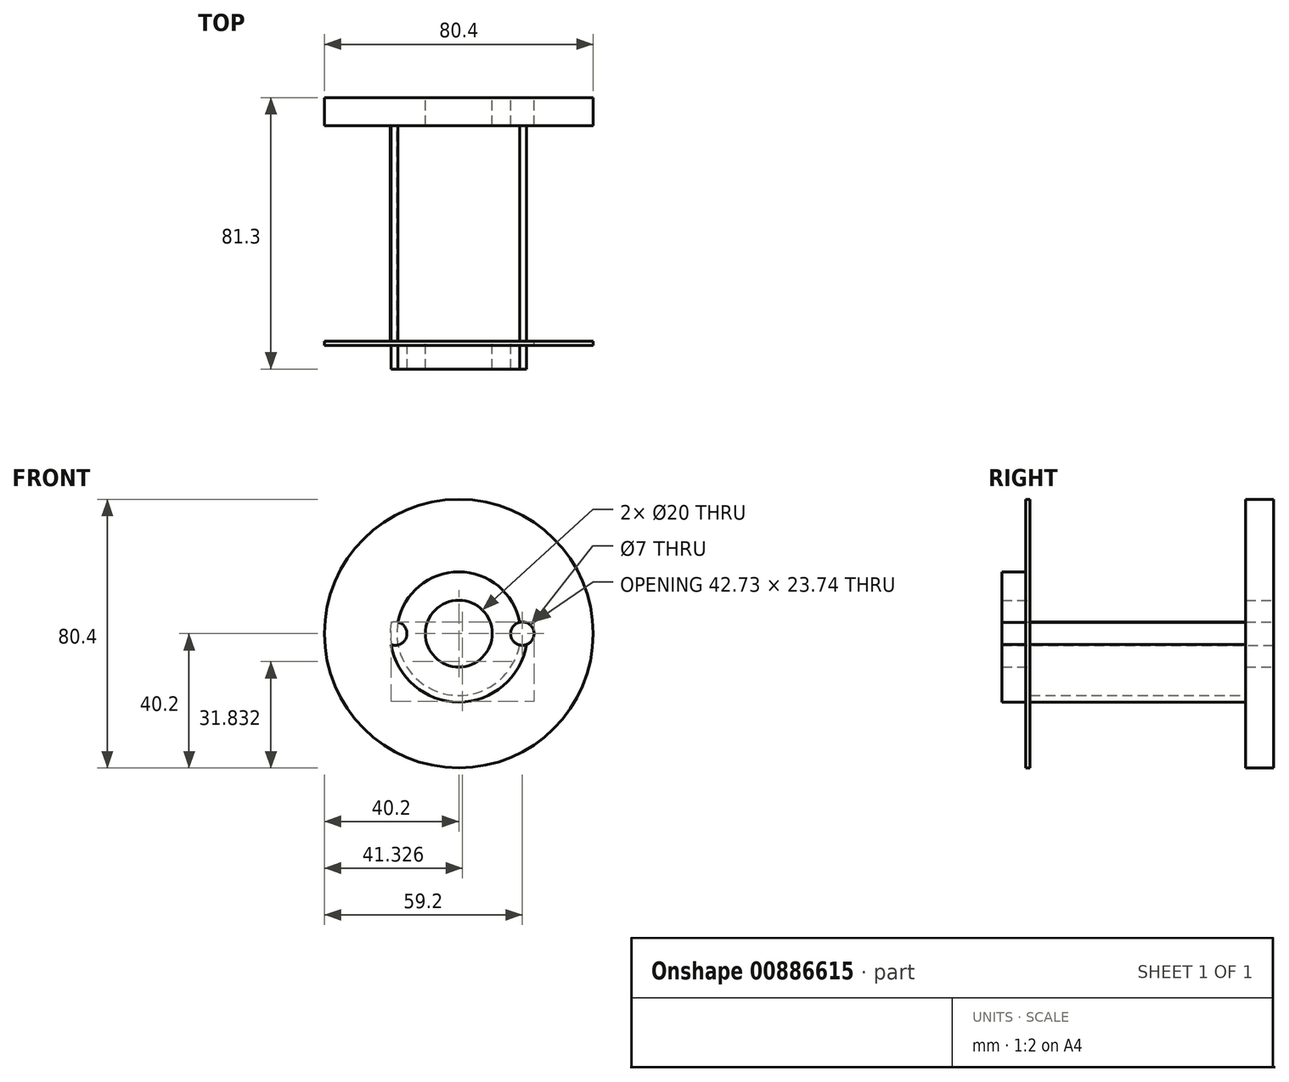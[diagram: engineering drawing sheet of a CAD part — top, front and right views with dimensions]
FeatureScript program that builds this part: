
annotation { "Feature Type Name" : "Feature", "Feature Type Description" : "" }
export const myFeature = defineFeature(function(context is Context, id is Id, definition is map)
    precondition{}
    {
        {
            var Q0;
            Q0=qCreatedBy(makeId("Front.planeOp"),FACE);
            var sketch = newSketch(context, id + "F0", { "sketchPlane" : qUnion([Q0])});
            skCircle(sketch, "E0", {"center": v(0, 0) * mm, "radius": 40.2 * mm});
            skCircle(sketch, "E1", {"center": v(0, 0) * mm, "radius": 10 * mm});
            skCircle(sketch, "E2", {"center": v(-19, 0) * mm, "radius": 3.5 * mm});
            skCircle(sketch, "E3.MirrorC", {"center": v(19, 0) * mm, "radius": 3.5 * mm});
            skCircle(sketch, "E4", {"center": v(0, 0) * mm, "radius": 20.5 * mm});
            skCircle(sketch, "E5.0", {"center": v(0, 0) * mm, "radius": 18.5 * mm});
            skSolve(sketch);
        }
        {
            var Q0;
            Q0=makeQuery(id+"F0.imprint","IMPRINT",FACE,{"disambiguationData":[TD([[makeQuery(id+"F0.imprint","IMPRINT",EDGE,{"derivedFrom":sQuery(id+"F0.wireOp",EDGE,"E1")}),-1.0]])]});
            var Q1;
            {var subQ0=sQuery(id+"F0.wireOp",EDGE,"E4");var subQ1=sQuery(id+"F0.wireOp",EDGE,"E3.MirrorC");var subQ2=makeQuery(id+"F0.imprint","INTERSECT",VERTEX,{"disambiguationData":[OD(0.0)],"derivedFrom":[subQ1,subQ0]});Q1=makeQuery(id+"F0.imprint","IMPRINT",FACE,{"disambiguationData":[TD([[makeQuery(id+"F0.imprint","IMPRINT",EDGE,{"disambiguationData":[TD([[subQ2,1.0]])],"derivedFrom":subQ1}),-1.0]])]});}
            var Q2;
            {var subQ0=sQuery(id+"F0.wireOp",EDGE,"E4");var subQ1=sQuery(id+"F0.wireOp",EDGE,"E3.MirrorC");var subQ2=makeQuery(id+"F0.imprint","INTERSECT",VERTEX,{"disambiguationData":[OD(0.0)],"derivedFrom":[subQ1,subQ0]});Q2=makeQuery(id+"F0.imprint","IMPRINT",FACE,{"disambiguationData":[TD([[makeQuery(id+"F0.imprint","IMPRINT",EDGE,{"disambiguationData":[TD([[subQ2,-1.0]])],"derivedFrom":subQ1}),-1.0]])]});}
            var Q3;
            Q3=makeQuery(id+"F0.imprint","IMPRINT",FACE,{"disambiguationData":[TD([[makeQuery(id+"F0.imprint","IMPRINT",EDGE,{"derivedFrom":sQuery(id+"F0.wireOp",EDGE,"E0")}),1.0]])]});
            var Q4;
            {var subQ0=sQuery(id+"F0.wireOp",EDGE,"E4");var subQ1=sQuery(id+"F0.wireOp",EDGE,"E2");var subQ2=makeQuery(id+"F0.imprint","INTERSECT",VERTEX,{"disambiguationData":[OD(0.0)],"derivedFrom":[subQ1,subQ0]});Q4=makeQuery(id+"F0.imprint","IMPRINT",FACE,{"disambiguationData":[TD([[makeQuery(id+"F0.imprint","IMPRINT",EDGE,{"disambiguationData":[TD([[subQ2,-1.0]])],"derivedFrom":subQ1}),1.0]])]});}
            var Q5;
            {var subQ0=sQuery(id+"F0.wireOp",EDGE,"E4");var subQ1=sQuery(id+"F0.wireOp",EDGE,"E2");var subQ2=makeQuery(id+"F0.imprint","INTERSECT",VERTEX,{"disambiguationData":[OD(0.0)],"derivedFrom":[subQ1,subQ0]});Q5=makeQuery(id+"F0.imprint","IMPRINT",FACE,{"disambiguationData":[TD([[makeQuery(id+"F0.imprint","IMPRINT",EDGE,{"disambiguationData":[TD([[subQ2,1.0]])],"derivedFrom":subQ1}),-1.0]])]});}
            var Q6;
            {var subQ0=sQuery(id+"F0.wireOp",EDGE,"E4");var subQ1=sQuery(id+"F0.wireOp",EDGE,"E2");var subQ2=makeQuery(id+"F0.imprint","INTERSECT",VERTEX,{"disambiguationData":[OD(0.0)],"derivedFrom":[subQ1,subQ0]});Q6=makeQuery(id+"F0.imprint","IMPRINT",FACE,{"disambiguationData":[TD([[makeQuery(id+"F0.imprint","IMPRINT",EDGE,{"disambiguationData":[TD([[subQ2,1.0]])],"derivedFrom":subQ1}),1.0]])]});}
            var Q7;
            {var subQ0=sQuery(id+"F0.wireOp",EDGE,"E5.0");var subQ1=sQuery(id+"F0.wireOp",EDGE,"E2");var subQ2=makeQuery(id+"F0.imprint","INTERSECT",VERTEX,{"disambiguationData":[OD(0.0)],"derivedFrom":[subQ1,subQ0]});Q7=makeQuery(id+"F0.imprint","IMPRINT",FACE,{"disambiguationData":[TD([[makeQuery(id+"F0.imprint","IMPRINT",EDGE,{"disambiguationData":[TD([[subQ2,1.0]])],"derivedFrom":subQ1}),1.0]])]});}
            var Q8;
            {var subQ0=sQuery(id+"F0.wireOp",EDGE,"E4");var subQ1=sQuery(id+"F0.wireOp",EDGE,"E2");var subQ2=makeQuery(id+"F0.imprint","INTERSECT",VERTEX,{"disambiguationData":[OD(1.0)],"derivedFrom":[subQ1,subQ0]});Q8=makeQuery(id+"F0.imprint","IMPRINT",FACE,{"disambiguationData":[TD([[makeQuery(id+"F0.imprint","IMPRINT",EDGE,{"disambiguationData":[TD([[subQ2,-1.0]])],"derivedFrom":subQ1}),-1.0]])]});}
            var Q9;
            {var subQ0=sQuery(id+"F0.wireOp",EDGE,"E5.0");var subQ1=sQuery(id+"F0.wireOp",EDGE,"E3.MirrorC");var subQ2=makeQuery(id+"F0.imprint","INTERSECT",VERTEX,{"disambiguationData":[OD(0.0)],"derivedFrom":[subQ1,subQ0]});Q9=makeQuery(id+"F0.imprint","IMPRINT",FACE,{"disambiguationData":[TD([[makeQuery(id+"F0.imprint","IMPRINT",EDGE,{"disambiguationData":[TD([[subQ2,1.0]])],"derivedFrom":subQ1}),-1.0]])]});}
            extrude(context, id + "F1", {"entities" : qUnion([Q0, Q1, Q2, Q3, Q4, Q5, Q6, Q7, Q8, Q9]), "endBound" : BoundingType.SYMMETRIC, "depth" : 81.3 * mm, "offsetDistance" : 25 * mm});
        }
        {
            var Q0;
            {var subQ0=sQuery(id+"F0.wireOp",EDGE,"E4");var subQ1=sQuery(id+"F0.wireOp",EDGE,"E3.MirrorC");var subQ2=makeQuery(id+"F0.imprint","INTERSECT",VERTEX,{"disambiguationData":[OD(0.0)],"derivedFrom":[subQ1,subQ0]});Q0=makeQuery(id+"F0.imprint","IMPRINT",FACE,{"disambiguationData":[TD([[makeQuery(id+"F0.imprint","IMPRINT",EDGE,{"disambiguationData":[TD([[subQ2,1.0]])],"derivedFrom":subQ1}),-1.0]])]});}
            var Q1;
            {var subQ0=sQuery(id+"F0.wireOp",EDGE,"E4");var subQ1=sQuery(id+"F0.wireOp",EDGE,"E3.MirrorC");var subQ2=makeQuery(id+"F0.imprint","INTERSECT",VERTEX,{"disambiguationData":[OD(0.0)],"derivedFrom":[subQ1,subQ0]});Q1=makeQuery(id+"F0.imprint","IMPRINT",FACE,{"disambiguationData":[TD([[makeQuery(id+"F0.imprint","IMPRINT",EDGE,{"disambiguationData":[TD([[subQ2,-1.0]])],"derivedFrom":subQ1}),-1.0]])]});}
            var Q2;
            {var subQ0=sQuery(id+"F0.wireOp",EDGE,"E4");var subQ1=sQuery(id+"F0.wireOp",EDGE,"E2");var subQ2=makeQuery(id+"F0.imprint","INTERSECT",VERTEX,{"disambiguationData":[OD(0.0)],"derivedFrom":[subQ1,subQ0]});Q2=makeQuery(id+"F0.imprint","IMPRINT",FACE,{"disambiguationData":[TD([[makeQuery(id+"F0.imprint","IMPRINT",EDGE,{"disambiguationData":[TD([[subQ2,-1.0]])],"derivedFrom":subQ1}),1.0]])]});}
            var Q3;
            {var subQ0=sQuery(id+"F0.wireOp",EDGE,"E4");var subQ1=sQuery(id+"F0.wireOp",EDGE,"E2");var subQ2=makeQuery(id+"F0.imprint","INTERSECT",VERTEX,{"disambiguationData":[OD(0.0)],"derivedFrom":[subQ1,subQ0]});Q3=makeQuery(id+"F0.imprint","IMPRINT",FACE,{"disambiguationData":[TD([[makeQuery(id+"F0.imprint","IMPRINT",EDGE,{"disambiguationData":[TD([[subQ2,1.0]])],"derivedFrom":subQ1}),1.0]])]});}
            var Q4;
            {var subQ0=sQuery(id+"F0.wireOp",EDGE,"E5.0");var subQ1=sQuery(id+"F0.wireOp",EDGE,"E2");var subQ2=makeQuery(id+"F0.imprint","INTERSECT",VERTEX,{"disambiguationData":[OD(0.0)],"derivedFrom":[subQ1,subQ0]});Q4=makeQuery(id+"F0.imprint","IMPRINT",FACE,{"disambiguationData":[TD([[makeQuery(id+"F0.imprint","IMPRINT",EDGE,{"disambiguationData":[TD([[subQ2,1.0]])],"derivedFrom":subQ1}),1.0]])]});}
            var Q5;
            {var subQ0=sQuery(id+"F0.wireOp",EDGE,"E5.0");var subQ1=sQuery(id+"F0.wireOp",EDGE,"E3.MirrorC");var subQ2=makeQuery(id+"F0.imprint","INTERSECT",VERTEX,{"disambiguationData":[OD(0.0)],"derivedFrom":[subQ1,subQ0]});Q5=makeQuery(id+"F0.imprint","IMPRINT",FACE,{"disambiguationData":[TD([[makeQuery(id+"F0.imprint","IMPRINT",EDGE,{"disambiguationData":[TD([[subQ2,1.0]])],"derivedFrom":subQ1}),-1.0]])]});}
            var Q6;
            Q6=sQuery(id+"F0.wireOp",EDGE,"E2");
            var Q7;
            Q7=sQuery(id+"F0.wireOp",EDGE,"E3.MirrorC");
            var Q8;
            Q8=makeQuery(id+"F1.opExtrude","CAP_FACE",FACE,{"disambiguationData":[OSD([sQuery(id+"F0.wireOp",EDGE,"E0"),sQuery(id+"F0.wireOp",EDGE,"E1")])],"isStart":false});
            extrude(context, id + "F2", {"entities" : qUnion([Q0, Q1, Q2, Q3, Q4, Q5]), "operationType" : NewBodyOperationType.REMOVE, "surfaceEntities" : qUnion([Q6, Q7]), "endBound" : BoundingType.UP_TO_SURFACE, "depth" : 7.2 * mm, "endBoundEntityFace" : qUnion([Q8]), "offsetDistance" : 25 * mm, "hasSecondDirection" : true, "secondDirectionOppositeDirection" : false, "secondDirectionDepth" : ((81.5 / 2) - 7.2) * mm});
        }
        {
            var Q0;
            Q0=makeQuery(id+"F0.imprint","IMPRINT",FACE,{"disambiguationData":[TD([[makeQuery(id+"F0.imprint","IMPRINT",EDGE,{"derivedFrom":sQuery(id+"F0.wireOp",EDGE,"E0")}),1.0]])]});
            var Q1;
            {var subQ0=sQuery(id+"F0.wireOp",EDGE,"E4");var subQ1=sQuery(id+"F0.wireOp",EDGE,"E2");var subQ2=makeQuery(id+"F0.imprint","INTERSECT",VERTEX,{"disambiguationData":[OD(0.0)],"derivedFrom":[subQ1,subQ0]});Q1=makeQuery(id+"F0.imprint","IMPRINT",FACE,{"disambiguationData":[TD([[makeQuery(id+"F0.imprint","IMPRINT",EDGE,{"disambiguationData":[TD([[subQ2,-1.0]])],"derivedFrom":subQ1}),1.0]])]});}
            var Q2;
            {var subQ0=sQuery(id+"F0.wireOp",EDGE,"E4");var subQ1=sQuery(id+"F0.wireOp",EDGE,"E3.MirrorC");var subQ2=makeQuery(id+"F0.imprint","INTERSECT",VERTEX,{"disambiguationData":[OD(0.0)],"derivedFrom":[subQ1,subQ0]});Q2=makeQuery(id+"F0.imprint","IMPRINT",FACE,{"disambiguationData":[TD([[makeQuery(id+"F0.imprint","IMPRINT",EDGE,{"disambiguationData":[TD([[subQ2,-1.0]])],"derivedFrom":subQ1}),-1.0]])]});}
            extrude(context, id + "F3", {"entities" : qUnion([Q0, Q1, Q2]), "operationType" : NewBodyOperationType.REMOVE, "endBound" : BoundingType.SYMMETRIC, "depth" : (81.5 - 8.5 * 2) * mm, "offsetDistance" : 25 * mm, "hasSecondDirection" : true, "secondDirectionOppositeDirection" : false, "secondDirectionDepth" : 8.5 * mm});
        }
        {
            var Q0;
            Q0=makeQuery(id+"F0.imprint","IMPRINT",FACE,{"disambiguationData":[TD([[makeQuery(id+"F0.imprint","IMPRINT",EDGE,{"derivedFrom":sQuery(id+"F0.wireOp",EDGE,"E1")}),-1.0]])]});
            var Q1;
            {var subQ0=sQuery(id+"F0.wireOp",EDGE,"E5.0");var subQ1=sQuery(id+"F0.wireOp",EDGE,"E2");var subQ2=makeQuery(id+"F0.imprint","INTERSECT",VERTEX,{"disambiguationData":[OD(0.0)],"derivedFrom":[subQ1,subQ0]});Q1=makeQuery(id+"F0.imprint","IMPRINT",FACE,{"disambiguationData":[TD([[makeQuery(id+"F0.imprint","IMPRINT",EDGE,{"disambiguationData":[TD([[subQ2,1.0]])],"derivedFrom":subQ1}),1.0]])]});}
            var Q2;
            {var subQ0=sQuery(id+"F0.wireOp",EDGE,"E5.0");var subQ1=sQuery(id+"F0.wireOp",EDGE,"E3.MirrorC");var subQ2=makeQuery(id+"F0.imprint","INTERSECT",VERTEX,{"disambiguationData":[OD(0.0)],"derivedFrom":[subQ1,subQ0]});Q2=makeQuery(id+"F0.imprint","IMPRINT",FACE,{"disambiguationData":[TD([[makeQuery(id+"F0.imprint","IMPRINT",EDGE,{"disambiguationData":[TD([[subQ2,1.0]])],"derivedFrom":subQ1}),-1.0]])]});}
            var Q3;
            Q3=sQuery(id+"F0.wireOp",EDGE,"E5.0");
            extrude(context, id + "F4", {"entities" : qUnion([Q0, Q1, Q2]), "operationType" : NewBodyOperationType.REMOVE, "surfaceEntities" : qUnion([Q3]), "endBound" : BoundingType.SYMMETRIC, "depth" : (81.5 - 8.5 * 2) * mm, "offsetDistance" : 25 * mm, "hasSecondDirection" : true, "secondDirectionOppositeDirection" : false, "secondDirectionDepth" : 8.5 * mm});
        }
    });
